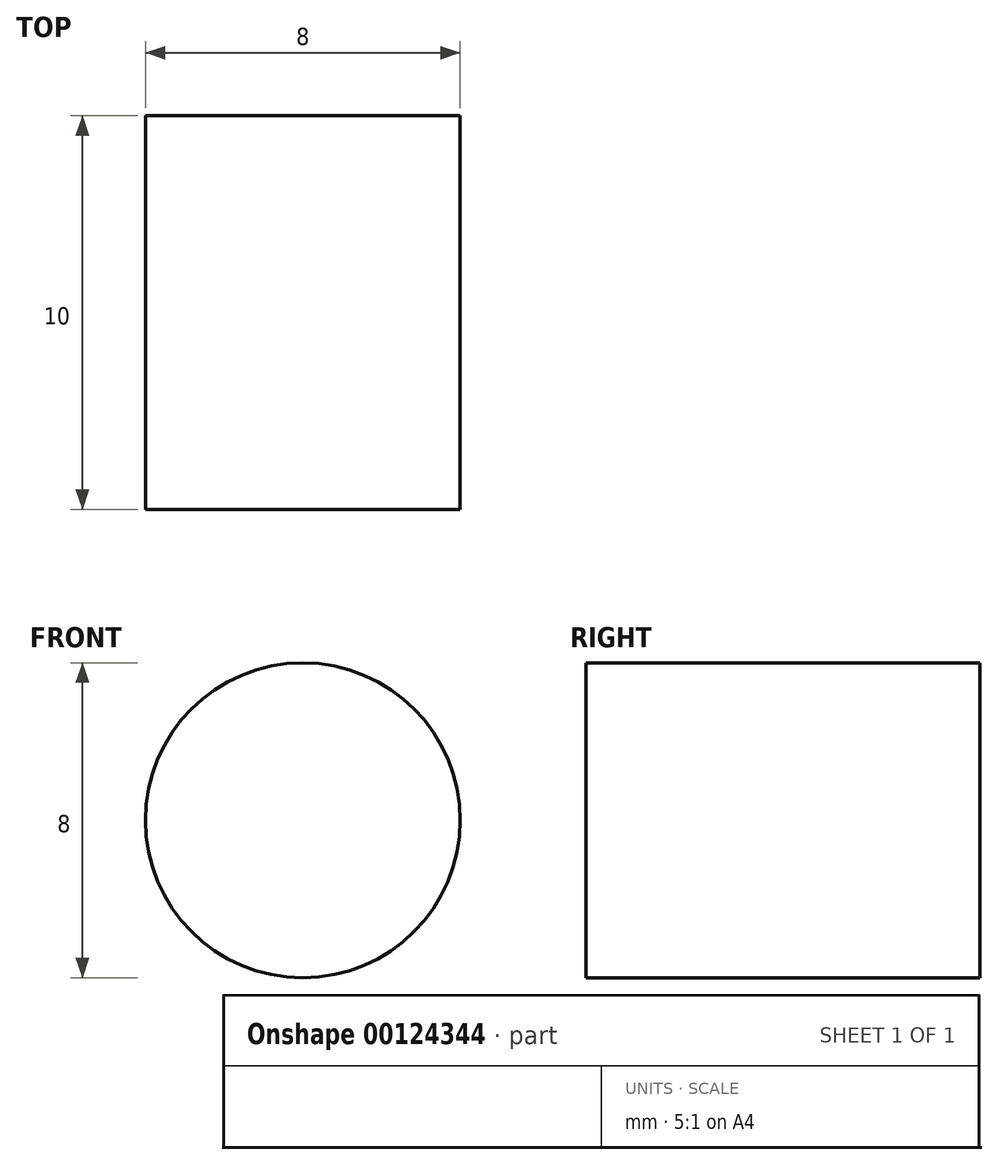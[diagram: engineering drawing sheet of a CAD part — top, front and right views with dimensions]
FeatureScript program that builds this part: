
annotation { "Feature Type Name" : "Feature", "Feature Type Description" : "" }
export const myFeature = defineFeature(function(context is Context, id is Id, definition is map)
    precondition{}
    {
        {
            var Q0;
            Q0=qCreatedBy(makeId("Front.planeOp"),FACE);
            var sketch = newSketch(context, id + "F0", { "sketchPlane" : qUnion([Q0])});
            skCircle(sketch, "E0", {"center": v(0, 0) * mm, "radius": 4 * mm});
            skSolve(sketch);
        }
        {
            var Q0;
            Q0 = qSketchRegion(id + "F0", true);
            extrude(context, id + "F1", {"entities" : qUnion([Q0]), "depth" : 10 * mm});
        }
    });
